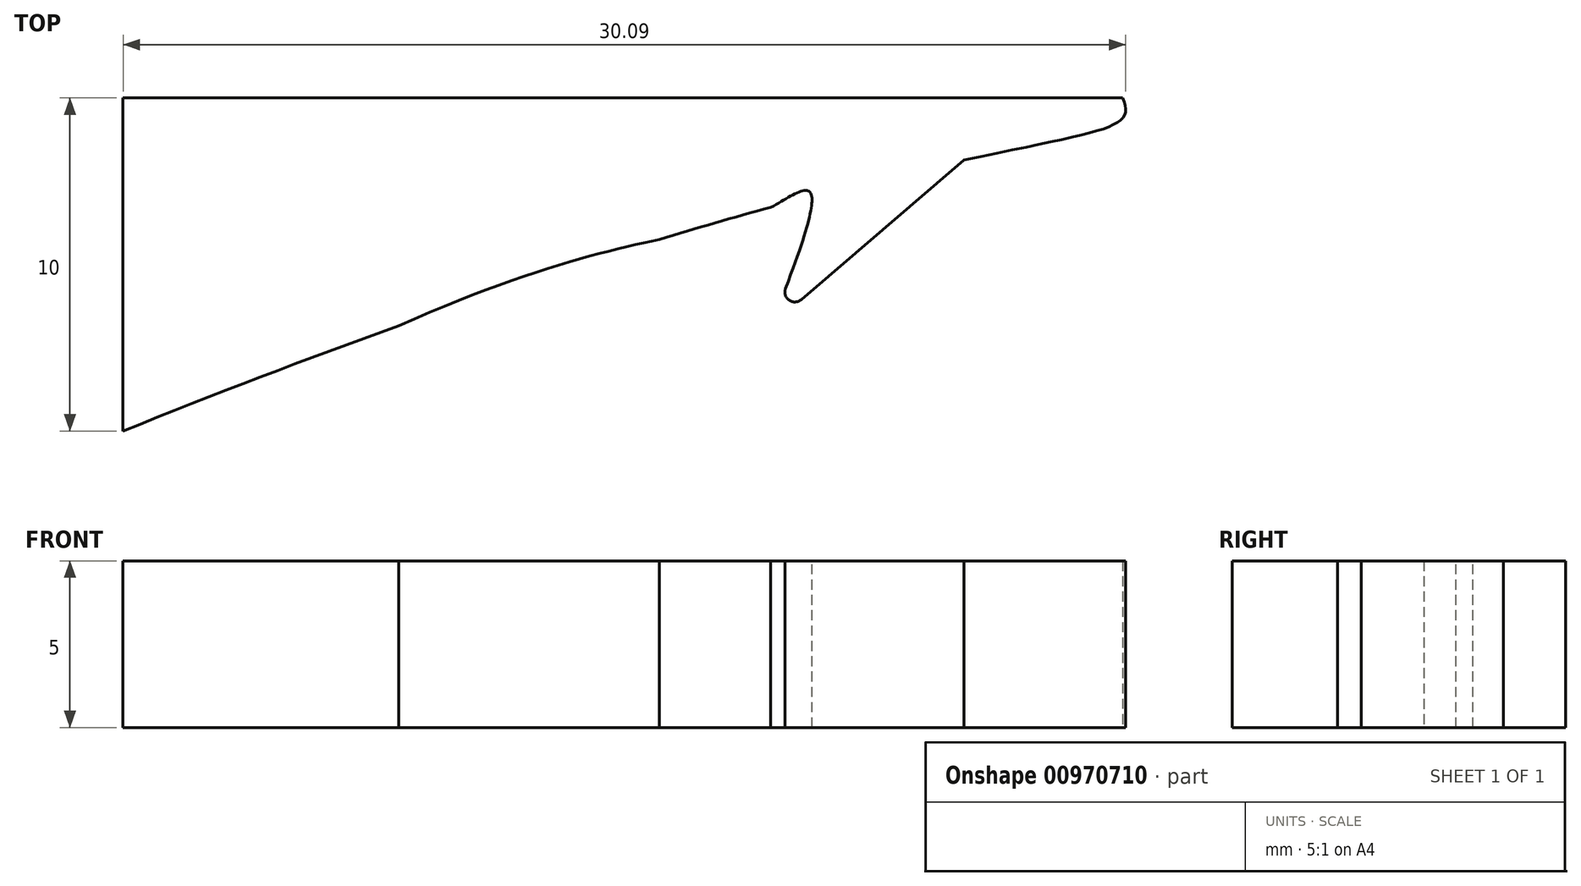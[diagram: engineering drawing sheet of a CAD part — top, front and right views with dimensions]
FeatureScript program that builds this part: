
annotation { "Feature Type Name" : "Feature", "Feature Type Description" : "" }
export const myFeature = defineFeature(function(context is Context, id is Id, definition is map)
    precondition{}
    {
        {
            var Q0;
            Q0=qCreatedBy(makeId("Top.planeOp"),FACE);
            var sketch = newSketch(context, id + "F0", { "sketchPlane" : qUnion([Q0])});
            skLineSegment(sketch, "E0", {"start": v(-12.84, 0) * mm, "end": v(-12.84, 10) * mm});
            skLineSegment(sketch, "E1", {"start": v(-12.84, 10) * mm, "end": v(17.16, 10) * mm});
            skFitSpline(sketch, "E2", {"points": [v(-12.84, 0) * mm, v(17.16, 10) * mm, v(12.52, 13.62) * mm], "startDerivative": vector(106.27, 42.93) * mm, "endDerivative": vector(-24.15, 11.66) * mm});
            skLineSegment(sketch, "E3", {"start": v(12.4, 8.13) * mm, "end": v(6.6, 3.16) * mm});
            skFitSpline(sketch, "E4", {"points": [v(6.6, 3.16) * mm, v(6.6, 6.72) * mm, v(-4.57, 3.16) * mm], "startDerivative": vector(17.74, 44.07) * mm, "endDerivative": vector(-30.86, -13.74) * mm});
            skSolve(sketch);
        }
        {
            var Q0;
            {var subQ4=sQuery(id+"F0.wireOp",EDGE,"E0");Q0=makeQuery(id+"F0.imprint","IMPRINT",FACE,{"disambiguationData":[TD([[makeQuery(id+"F0.imprint","IMPRINT",EDGE,{"derivedFrom":subQ4}),-1.0]])]});}
            var Q1;
            {var subQ0=sQuery(id+"F0.wireOp",EDGE,"E3");Q1=makeQuery(id+"F0.imprint","IMPRINT",FACE,{"disambiguationData":[TD([[makeQuery(id+"F0.imprint","IMPRINT",EDGE,{"derivedFrom":subQ0}),-1.0]])]});}
            extrude(context, id + "F1", {"entities" : qUnion([Q0, Q1]), "depth" : 5 * mm, "offsetDistance" : 25 * mm});
        }
        {
            var Q0;
            Q0=makeQuery(id+"F1.opExtrude","SWEPT_EDGE",EDGE,{"disambiguationData":[OSD([sQuery(id+"F0.wireOp",EDGE,"E3"),sQuery(id+"F0.wireOp",EDGE,"E4")])]});
            fillet(context, id + "F2", {"entities" : qUnion([Q0]), "radius" : .3 * mm, "tangentPropagation" : true, "allowEdgeOverflow" : false});
        }
    });
